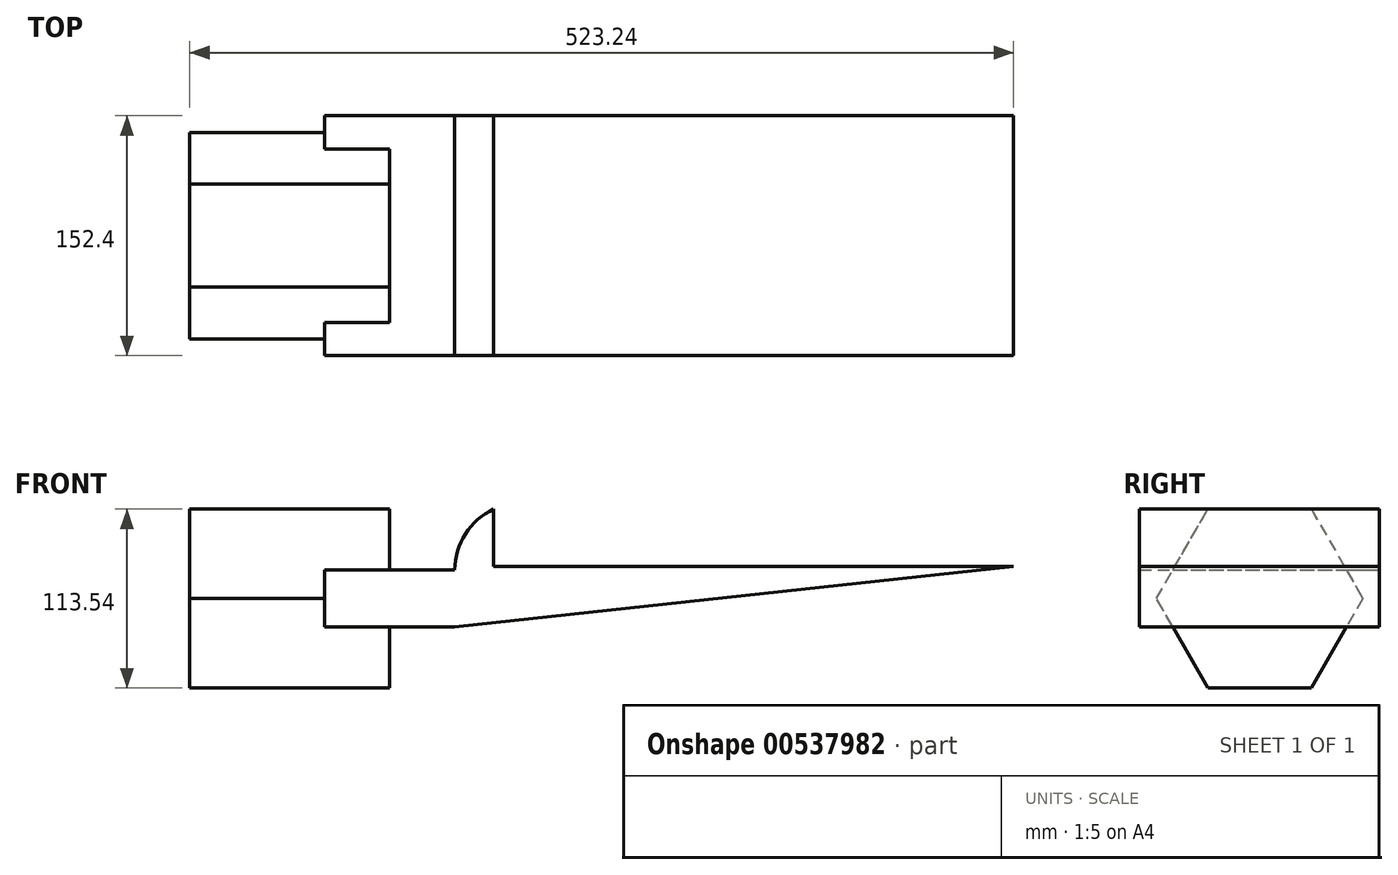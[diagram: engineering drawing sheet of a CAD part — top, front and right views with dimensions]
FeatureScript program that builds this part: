
annotation { "Feature Type Name" : "Feature", "Feature Type Description" : "" }
export const myFeature = defineFeature(function(context is Context, id is Id, definition is map)
    precondition{}
    {
        {
            var Q0;
            Q0=qCreatedBy(makeId("Front.planeOp"),FACE);
            var sketch = newSketch(context, id + "F0", { "sketchPlane" : qUnion([Q0])});
            skLineSegment(sketch, "E0.bottom", {"start": v(-41.28, 18.13) * mm, "end": v(41.28, 18.13) * mm});
            skLineSegment(sketch, "E0.top", {"start": v(-41.28, -18.13) * mm, "end": v(41.28, -18.13) * mm});
            skLineSegment(sketch, "E0.left", {"start": v(-41.28, 18.13) * mm, "end": v(-41.28, -18.13) * mm});
            skLineSegment(sketch, "E0.right", {"start": v(41.28, 18.13) * mm, "end": v(41.28, -18.13) * mm});
            skPoint(sketch, "E0.middle", {"position": v(0, 0) * mm});
            skLineSegment(sketch, "E1.bottom", {"start": v(396.24, 56.75) * mm, "end": v(66.04, 56.75) * mm});
            skLineSegment(sketch, "E1.top", {"start": v(396.24, 20.2) * mm, "end": v(66.04, 20.2) * mm});
            skLineSegment(sketch, "E1.left", {"start": v(396.24, 56.75) * mm, "end": v(396.24, 20.2) * mm});
            skLineSegment(sketch, "E1.right", {"start": v(66.04, 56.75) * mm, "end": v(66.04, 20.2) * mm});
            skPoint(sketch, "E1.middle", {"position": v(231.14, 38.47) * mm});
            skPoint(sketch, "E2.endSnap0", {"position": v(231.14, 56.75) * mm});
            skArc(sketch, "E3", {"start": v(41.28, 18.13) * mm, "mid": v(48, 41.07) * mm, "end": v(66.04, 56.75) * mm});
            skLineSegment(sketch, "E4", {"start": v(41.27, -18.13) * mm, "end": v(396.24, 20.2) * mm});
            skFitSpline(sketch, "E5", {"points": [v(-41.28, 18.13) * mm, v(66.04, 56.75) * mm, v(83.77, 18.13) * mm], "startDerivative": vector(211.95, 113.14) * mm, "endDerivative": vector(22.9, -133) * mm});
            skSolve(sketch);
        }
        {
            var Q0;
            Q0=makeQuery(id+"F0.imprint","IMPRINT",FACE,{"disambiguationData":[TD([[makeQuery(id+"F0.imprint","IMPRINT",EDGE,{"derivedFrom":sQuery(id+"F0.wireOp",EDGE,"E0.right")}),1.0]])]});
            var Q1;
            Q1=makeQuery(id+"F0.imprint","IMPRINT",FACE,{"disambiguationData":[TD([[makeQuery(id+"F0.imprint","IMPRINT",EDGE,{"derivedFrom":sQuery(id+"F0.wireOp",EDGE,"E0.bottom")}),-1.0]])]});
            extrude(context, id + "F1", {"entities" : qUnion([Q0, Q1]), "depth" : 76.2 * mm, "offsetDistance" : 25.4 * mm, "hasSecondDirection" : true, "secondDirectionOppositeDirection" : true, "secondDirectionDepth" : 76.2 * mm});
        }
        {
            var Q0;
            Q0=qCreatedBy(makeId("Right.planeOp"),FACE);
            var sketch = newSketch(context, id + "F2", { "sketchPlane" : qUnion([Q0])});
            skCircle(sketch, "E6.cCircle", {"center": v(0, 0) * mm, "radius": 56.77 * mm, "construction": true});
            skLineSegment(sketch, "E6.0", {"start": v(-32.78, 56.77) * mm, "end": v(32.78, 56.77) * mm});
            skLineSegment(sketch, "E6.1", {"start": v(32.78, 56.77) * mm, "end": v(65.55, 0) * mm});
            skLineSegment(sketch, "E6.2", {"start": v(65.55, 0) * mm, "end": v(32.78, -56.77) * mm});
            skLineSegment(sketch, "E6.3", {"start": v(32.78, -56.77) * mm, "end": v(-32.78, -56.77) * mm});
            skLineSegment(sketch, "E6.4", {"start": v(-32.78, -56.77) * mm, "end": v(-65.55, 0) * mm});
            skLineSegment(sketch, "E6.5", {"start": v(-65.55, 0) * mm, "end": v(-32.78, 56.77) * mm});
            skPoint(sketch, "E6.0.midPoint", {"position": v(0, 56.77) * mm});
            skSolve(sketch);
        }
        {
            var Q0;
            Q0 = qSketchRegion(id + "F2", true);
            extrude(context, id + "F3", {"entities" : qUnion([Q0]), "operationType" : NewBodyOperationType.ADD, "depth" : 0 * mm, "offsetDistance" : 25.4 * mm, "hasSecondDirection" : true, "secondDirectionOppositeDirection" : true, "secondDirectionDepth" : 127 * mm});
        }
    });
